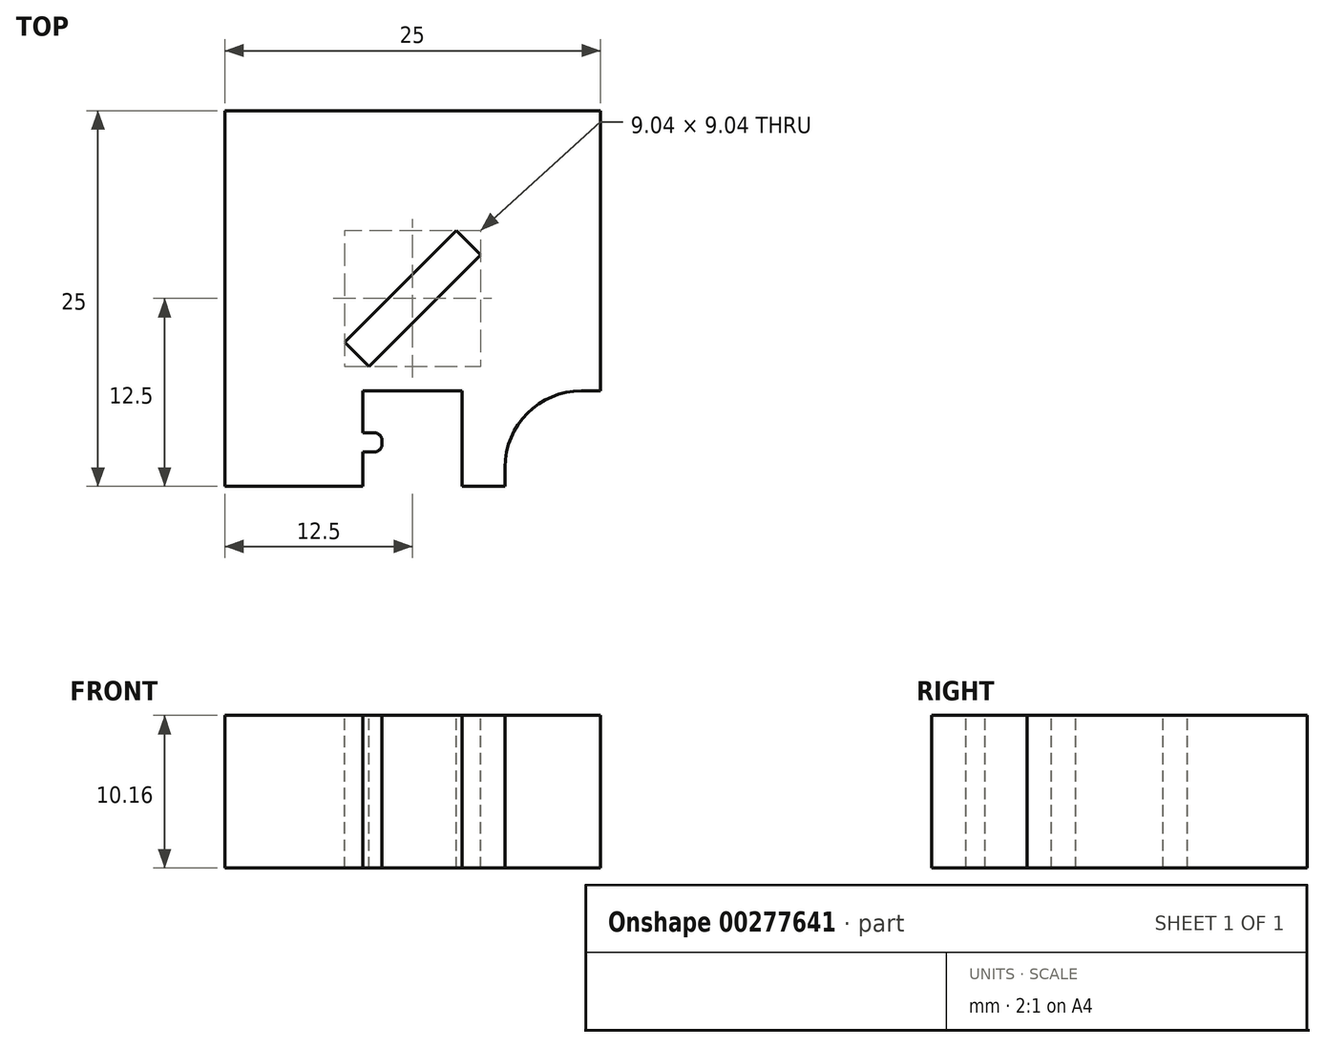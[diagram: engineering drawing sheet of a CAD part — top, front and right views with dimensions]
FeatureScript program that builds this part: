
annotation { "Feature Type Name" : "Feature", "Feature Type Description" : "" }
export const myFeature = defineFeature(function(context is Context, id is Id, definition is map)
    precondition{}
    {
        {
            var Q0;
            Q0=qCreatedBy(makeId("Top.planeOp"),FACE);
            var sketch = newSketch(context, id + "F0", { "sketchPlane" : qUnion([Q0])});
            skLineSegment(sketch, "E0.bottom", {"start": v(12.5, -12.5) * mm, "end": v(-12.5, -12.5) * mm});
            skLineSegment(sketch, "E0.top", {"start": v(12.5, 12.5) * mm, "end": v(-12.5, 12.5) * mm});
            skLineSegment(sketch, "E0.left", {"start": v(12.5, -12.5) * mm, "end": v(12.5, 12.5) * mm});
            skLineSegment(sketch, "E0.right", {"start": v(-12.5, -12.5) * mm, "end": v(-12.5, 12.5) * mm});
            skPoint(sketch, "E0.middle", {"position": v(0, 0) * mm});
            skSolve(sketch);
        }
        {
            var Q0;
            Q0=makeQuery(id+"F0.imprint","IMPRINT",FACE,{"disambiguationData":[TD([[makeQuery(id+"F0.imprint","IMPRINT",EDGE,{"derivedFrom":sQuery(id+"F0.wireOp",EDGE,"E0.bottom")}),-1.0]])]});
            extrude(context, id + "F1", {"entities" : qUnion([Q0]), "depth" : 10.16 * mm});
        }
        {
            var Q0;
            Q0=makeQuery(id+"F1.opExtrude","CAP_FACE",FACE,{"disambiguationData":[OSD([sQuery(id+"F0.wireOp",EDGE,"E0.bottom"),sQuery(id+"F0.wireOp",EDGE,"E0.top"),sQuery(id+"F0.wireOp",EDGE,"E0.left"),sQuery(id+"F0.wireOp",EDGE,"E0.right")])],"isStart":false});
            var sketch = newSketch(context, id + "F2", { "sketchPlane" : qUnion([Q0])});
            skLineSegment(sketch, "E1.bottom", {"start": v(-3.3, -12.5) * mm, "end": v(3.3, -12.5) * mm});
            skLineSegment(sketch, "E1.top", {"start": v(-3.3, -6.15) * mm, "end": v(3.3, -6.15) * mm});
            skLineSegment(sketch, "E1.left", {"start": v(-3.3, -12.5) * mm, "end": v(-3.3, -6.15) * mm});
            skLineSegment(sketch, "E1.right", {"start": v(3.3, -12.5) * mm, "end": v(3.3, -6.15) * mm});
            skSolve(sketch);
        }
        {
            var Q0;
            Q0=makeQuery(id+"F2.imprint","IMPRINT",FACE,{"disambiguationData":[TD([[makeQuery(id+"F2.imprint","IMPRINT",EDGE,{"derivedFrom":sQuery(id+"F2.wireOp",EDGE,"E1.bottom")}),-1.0]])]});
            extrude(context, id + "F3", {"entities" : qUnion([Q0]), "operationType" : NewBodyOperationType.REMOVE, "oppositeDirection" : true, "depth" : 25.4 * mm});
        }
        {
            var Q0;
            Q0=makeQuery(id+"F1.opExtrude","CAP_FACE",FACE,{"disambiguationData":[OSD([sQuery(id+"F0.wireOp",EDGE,"E0.bottom"),sQuery(id+"F0.wireOp",EDGE,"E0.top"),sQuery(id+"F0.wireOp",EDGE,"E0.left"),sQuery(id+"F0.wireOp",EDGE,"E0.right")])],"isStart":false});
            var sketch = newSketch(context, id + "F4", { "sketchPlane" : qUnion([Q0])});
            skLineSegment(sketch, "E2.bottom", {"start": v(-3.3, -8.94) * mm, "end": v(-2.03, -8.94) * mm});
            skLineSegment(sketch, "E2.top", {"start": v(-3.3, -10.21) * mm, "end": v(-2.03, -10.21) * mm});
            skLineSegment(sketch, "E2.left", {"start": v(-3.3, -8.94) * mm, "end": v(-3.3, -10.21) * mm});
            skLineSegment(sketch, "E2.right", {"start": v(-2.03, -8.94) * mm, "end": v(-2.03, -10.21) * mm});
            skSolve(sketch);
        }
        {
            var Q0;
            Q0=makeQuery(id+"F4.imprint","IMPRINT",FACE,{"disambiguationData":[TD([[makeQuery(id+"F4.imprint","IMPRINT",EDGE,{"derivedFrom":sQuery(id+"F4.wireOp",EDGE,"E2.bottom")}),-1.0]])]});
            var Q1;
            Q1=makeQuery(id+"F1.opExtrude","CAP_FACE",FACE,{"disambiguationData":[OSD([sQuery(id+"F0.wireOp",EDGE,"E0.bottom"),sQuery(id+"F0.wireOp",EDGE,"E0.top"),sQuery(id+"F0.wireOp",EDGE,"E0.left"),sQuery(id+"F0.wireOp",EDGE,"E0.right")])],"isStart":true});
            extrude(context, id + "F5", {"entities" : qUnion([Q0]), "operationType" : NewBodyOperationType.ADD, "endBound" : BoundingType.UP_TO_SURFACE, "oppositeDirection" : true, "endBoundEntityFace" : qUnion([Q1]), "depth" : 25.4 * mm});
        }
        {
            var Q0;
            Q0=qCreatedBy(makeId("Front.planeOp"),FACE);
            var sketch = newSketch(context, id + "F6", { "sketchPlane" : qUnion([Q0])});
            skLineSegment(sketch, "E3", {"start": v(0, 0) * mm, "end": v(0, 39.35) * mm});
            skSolve(sketch);
        }
        {
            var Q0;
            {var subQ0=sQuery(id+"F4.wireOp",EDGE,"E2.right");var subQ1=sQuery(id+"F4.wireOp",EDGE,"E2.left");var subQ2=sQuery(id+"F4.wireOp",EDGE,"E2.top");var subQ3=sQuery(id+"F4.wireOp",EDGE,"E2.bottom");Q0=makeQuery(id+"FZ99muYWaTXzHZh_1.3.F9qQpSXjTnUJ7Ic_1.1.F5.boolean.opBoolean","MERGE",FACE,{"derivedFrom":[makeQuery(id+"FZ99muYWaTXzHZh_1.3.F5.boolean.opBoolean","MERGE",FACE,{"derivedFrom":[makeQuery(id+"FZ99muYWaTXzHZh_1.2.F9qQpSXjTnUJ7Ic_1.1.F5.boolean.opBoolean","MERGE",FACE,{"derivedFrom":[makeQuery(id+"FZ99muYWaTXzHZh_1.2.F5.boolean.opBoolean","MERGE",FACE,{"derivedFrom":[makeQuery(id+"FZ99muYWaTXzHZh_1.1.F5.boolean.opBoolean","MERGE",FACE,{"derivedFrom":[makeQuery(id+"F9qQpSXjTnUJ7Ic_1.1.F5.boolean.opBoolean","MERGE",FACE,{"derivedFrom":[makeQuery(id+"F5.boolean.opBoolean","MERGE",FACE,{"derivedFrom":[makeQuery(id+"F1.opExtrude","CAP_FACE",FACE,{"disambiguationData":[OSD([sQuery(id+"F0.wireOp",EDGE,"E0.bottom"),sQuery(id+"F0.wireOp",EDGE,"E0.top"),sQuery(id+"F0.wireOp",EDGE,"E0.left"),sQuery(id+"F0.wireOp",EDGE,"E0.right")])],"isStart":false}),makeQuery(id+"F5.opExtrude","CAP_FACE",FACE,{"disambiguationData":[OSD([subQ3,subQ2,subQ1,subQ0])],"isStart":true})]}),makeQuery(id+"F9qQpSXjTnUJ7Ic_1.1.F5.opExtrude","CAP_FACE",FACE,{"disambiguationData":[OSD([subQ3,subQ2,subQ1,subQ0])],"isStart":true})]}),makeQuery(id+"FZ99muYWaTXzHZh_1.1.F5.opExtrude","CAP_FACE",FACE,{"disambiguationData":[OSD([subQ3,subQ2,subQ1,subQ0])],"isStart":true})]}),makeQuery(id+"FZ99muYWaTXzHZh_1.2.F5.opExtrude","CAP_FACE",FACE,{"disambiguationData":[OSD([subQ3,subQ2,subQ1,subQ0])],"isStart":true})]}),makeQuery(id+"FZ99muYWaTXzHZh_1.2.F9qQpSXjTnUJ7Ic_1.1.F5.opExtrude","CAP_FACE",FACE,{"disambiguationData":[OSD([subQ3,subQ2,subQ1,subQ0])],"isStart":true})]}),makeQuery(id+"FZ99muYWaTXzHZh_1.3.F5.opExtrude","CAP_FACE",FACE,{"disambiguationData":[OSD([subQ3,subQ2,subQ1,subQ0])],"isStart":true})]}),makeQuery(id+"FZ99muYWaTXzHZh_1.3.F9qQpSXjTnUJ7Ic_1.1.F5.opExtrude","CAP_FACE",FACE,{"disambiguationData":[OSD([subQ3,subQ2,subQ1,subQ0])],"isStart":true})]});}
            var sketch = newSketch(context, id + "F7", { "sketchPlane" : qUnion([Q0])});
            skLineSegment(sketch, "E4.bottom", {"start": v(-9.96, -3.3) * mm, "end": v(-8.7, -3.3) * mm});
            skLineSegment(sketch, "E4.top", {"start": v(-9.96, -2.03) * mm, "end": v(-8.7, -2.03) * mm});
            skLineSegment(sketch, "E4.left", {"start": v(-9.96, -3.3) * mm, "end": v(-9.96, -2.03) * mm});
            skLineSegment(sketch, "E4.right", {"start": v(-8.7, -3.3) * mm, "end": v(-8.7, -2.03) * mm});
            skSolve(sketch);
        }
        {
            var Q0;
            Q0=makeQuery(id+"F7.imprint","IMPRINT",FACE,{"disambiguationData":[TD([[makeQuery(id+"F7.imprint","IMPRINT",EDGE,{"derivedFrom":sQuery(id+"F7.wireOp",EDGE,"E4.bottom")}),1.0]])]});
            var Q1;
            {var subQ0=sQuery(id+"F0.wireOp",EDGE,"E0.right");var subQ1=sQuery(id+"F0.wireOp",EDGE,"E0.left");var subQ2=sQuery(id+"F0.wireOp",EDGE,"E0.top");var subQ3=sQuery(id+"F0.wireOp",EDGE,"E0.bottom");Q1=makeQuery(id+"FZ99muYWaTXzHZh_1.3.F9qQpSXjTnUJ7Ic_1.1.F5.boolean.opBoolean","MERGE",FACE,{"derivedFrom":[makeQuery(id+"FZ99muYWaTXzHZh_1.3.F5.boolean.opBoolean","MERGE",FACE,{"derivedFrom":[makeQuery(id+"FZ99muYWaTXzHZh_1.2.F9qQpSXjTnUJ7Ic_1.1.F5.boolean.opBoolean","MERGE",FACE,{"derivedFrom":[makeQuery(id+"FZ99muYWaTXzHZh_1.2.F5.boolean.opBoolean","MERGE",FACE,{"derivedFrom":[makeQuery(id+"FZ99muYWaTXzHZh_1.1.F5.boolean.opBoolean","MERGE",FACE,{"derivedFrom":[makeQuery(id+"F9qQpSXjTnUJ7Ic_1.1.F5.boolean.opBoolean","MERGE",FACE,{"derivedFrom":[makeQuery(id+"F5.boolean.opBoolean","MERGE",FACE,{"derivedFrom":[makeQuery(id+"F1.opExtrude","CAP_FACE",FACE,{"disambiguationData":[OSD([subQ3,subQ2,subQ1,subQ0])],"isStart":true}),makeQuery(id+"F5.opExtrude","CAP_FACE",FACE,{"disambiguationData":[OSD([subQ3,subQ2,subQ1,subQ0])],"isStart":false})]}),makeQuery(id+"F9qQpSXjTnUJ7Ic_1.1.F5.opExtrude","CAP_FACE",FACE,{"disambiguationData":[OSD([subQ3,subQ2,subQ1,subQ0])],"isStart":false})]}),makeQuery(id+"FZ99muYWaTXzHZh_1.1.F5.opExtrude","CAP_FACE",FACE,{"disambiguationData":[OSD([subQ3,subQ2,subQ1,subQ0])],"isStart":false})]}),makeQuery(id+"FZ99muYWaTXzHZh_1.2.F5.opExtrude","CAP_FACE",FACE,{"disambiguationData":[OSD([subQ3,subQ2,subQ1,subQ0])],"isStart":false})]}),makeQuery(id+"FZ99muYWaTXzHZh_1.2.F9qQpSXjTnUJ7Ic_1.1.F5.opExtrude","CAP_FACE",FACE,{"disambiguationData":[OSD([subQ3,subQ2,subQ1,subQ0])],"isStart":false})]}),makeQuery(id+"FZ99muYWaTXzHZh_1.3.F5.opExtrude","CAP_FACE",FACE,{"disambiguationData":[OSD([subQ3,subQ2,subQ1,subQ0])],"isStart":false})]}),makeQuery(id+"FZ99muYWaTXzHZh_1.3.F9qQpSXjTnUJ7Ic_1.1.F5.opExtrude","CAP_FACE",FACE,{"disambiguationData":[OSD([subQ3,subQ2,subQ1,subQ0])],"isStart":false})]});}
            extrude(context, id + "F8", {"entities" : qUnion([Q0]), "operationType" : NewBodyOperationType.ADD, "endBound" : BoundingType.UP_TO_SURFACE, "oppositeDirection" : true, "endBoundEntityFace" : qUnion([Q1]), "depth" : 25.4 * mm});
        }
        {
            var Q0;
            {var subQ0=sQuery(id+"F4.wireOp",EDGE,"E2.right");var subQ1=sQuery(id+"F4.wireOp",EDGE,"E2.left");var subQ2=sQuery(id+"F4.wireOp",EDGE,"E2.top");var subQ3=sQuery(id+"F4.wireOp",EDGE,"E2.bottom");Q0=makeQuery(id+"F8.boolean.opBoolean","MERGE",FACE,{"derivedFrom":[makeQuery(id+"FZ99muYWaTXzHZh_1.3.F9qQpSXjTnUJ7Ic_1.1.F5.boolean.opBoolean","MERGE",FACE,{"derivedFrom":[makeQuery(id+"FZ99muYWaTXzHZh_1.3.F5.boolean.opBoolean","MERGE",FACE,{"derivedFrom":[makeQuery(id+"FZ99muYWaTXzHZh_1.2.F9qQpSXjTnUJ7Ic_1.1.F5.boolean.opBoolean","MERGE",FACE,{"derivedFrom":[makeQuery(id+"FZ99muYWaTXzHZh_1.2.F5.boolean.opBoolean","MERGE",FACE,{"derivedFrom":[makeQuery(id+"FZ99muYWaTXzHZh_1.1.F5.boolean.opBoolean","MERGE",FACE,{"derivedFrom":[makeQuery(id+"F9qQpSXjTnUJ7Ic_1.1.F5.boolean.opBoolean","MERGE",FACE,{"derivedFrom":[makeQuery(id+"F5.boolean.opBoolean","MERGE",FACE,{"derivedFrom":[makeQuery(id+"F1.opExtrude","CAP_FACE",FACE,{"disambiguationData":[OSD([sQuery(id+"F0.wireOp",EDGE,"E0.bottom"),sQuery(id+"F0.wireOp",EDGE,"E0.top"),sQuery(id+"F0.wireOp",EDGE,"E0.left"),sQuery(id+"F0.wireOp",EDGE,"E0.right")])],"isStart":false}),makeQuery(id+"F5.opExtrude","CAP_FACE",FACE,{"disambiguationData":[OSD([subQ3,subQ2,subQ1,subQ0])],"isStart":true})]}),makeQuery(id+"F9qQpSXjTnUJ7Ic_1.1.F5.opExtrude","CAP_FACE",FACE,{"disambiguationData":[OSD([subQ3,subQ2,subQ1,subQ0])],"isStart":true})]}),makeQuery(id+"FZ99muYWaTXzHZh_1.1.F5.opExtrude","CAP_FACE",FACE,{"disambiguationData":[OSD([subQ3,subQ2,subQ1,subQ0])],"isStart":true})]}),makeQuery(id+"FZ99muYWaTXzHZh_1.2.F5.opExtrude","CAP_FACE",FACE,{"disambiguationData":[OSD([subQ3,subQ2,subQ1,subQ0])],"isStart":true})]}),makeQuery(id+"FZ99muYWaTXzHZh_1.2.F9qQpSXjTnUJ7Ic_1.1.F5.opExtrude","CAP_FACE",FACE,{"disambiguationData":[OSD([subQ3,subQ2,subQ1,subQ0])],"isStart":true})]}),makeQuery(id+"FZ99muYWaTXzHZh_1.3.F5.opExtrude","CAP_FACE",FACE,{"disambiguationData":[OSD([subQ3,subQ2,subQ1,subQ0])],"isStart":true})]}),makeQuery(id+"FZ99muYWaTXzHZh_1.3.F9qQpSXjTnUJ7Ic_1.1.F5.opExtrude","CAP_FACE",FACE,{"disambiguationData":[OSD([subQ3,subQ2,subQ1,subQ0])],"isStart":true})]}),makeQuery(id+"F8.opExtrude","CAP_FACE",FACE,{"disambiguationData":[OSD([sQuery(id+"F7.wireOp",EDGE,"E4.bottom"),sQuery(id+"F7.wireOp",EDGE,"E4.top"),sQuery(id+"F7.wireOp",EDGE,"E4.left"),sQuery(id+"F7.wireOp",EDGE,"E4.right")])],"isStart":true})]});}
            var sketch = newSketch(context, id + "F9", { "sketchPlane" : qUnion([Q0])});
            skLineSegment(sketch, "E5.bottom", {"start": v(12.5, -12.5) * mm, "end": v(6.15, -12.5) * mm});
            skLineSegment(sketch, "E5.top", {"start": v(12.5, -6.15) * mm, "end": v(6.15, -6.15) * mm});
            skLineSegment(sketch, "E5.left", {"start": v(12.5, -12.5) * mm, "end": v(12.5, -6.15) * mm});
            skLineSegment(sketch, "E5.right", {"start": v(6.15, -12.5) * mm, "end": v(6.15, -6.15) * mm});
            skSolve(sketch);
        }
        {
            var Q0;
            Q0=makeQuery(id+"F9.imprint","IMPRINT",FACE,{"disambiguationData":[TD([[makeQuery(id+"F9.imprint","IMPRINT",EDGE,{"derivedFrom":sQuery(id+"F9.wireOp",EDGE,"E5.bottom")}),-1.0]])]});
            extrude(context, id + "F10", {"entities" : qUnion([Q0]), "operationType" : NewBodyOperationType.REMOVE, "oppositeDirection" : true, "depth" : 25.4 * mm});
        }
        {
            var Q0;
            Q0=makeQuery(id+"F10.boolean.opBoolean","COPY",EDGE,{"derivedFrom":makeQuery(id+"F10.opExtrude","SWEPT_EDGE",EDGE,{"disambiguationData":[OSD([sQuery(id+"F9.wireOp",EDGE,"E5.top"),sQuery(id+"F9.wireOp",EDGE,"E5.right")])]})});
            fillet(context, id + "F11", {"entities" : qUnion([Q0]), "radius" : 5.08 * mm, "tangentPropagation" : true, "allowEdgeOverflow" : false});
        }
        {
            var Q0;
            {var subQ44=sQuery(id+"F7.wireOp",EDGE,"E4.bottom");Q0=makeQuery(id+"F7.imprint","IMPRINT",FACE,{"disambiguationData":[TD([[makeQuery(id+"F7.imprint","IMPRINT",EDGE,{"derivedFrom":subQ44}),-1.0]])]});}
            var sketch = newSketch(context, id + "F12", { "sketchPlane" : qUnion([Q0])});
            skLineSegment(sketch, "E6", {"start": v(-4.52, -2.9) * mm, "end": v(2.9, 4.52) * mm});
            skLineSegment(sketch, "E7", {"start": v(2.9, 4.52) * mm, "end": v(4.52, 2.9) * mm});
            skLineSegment(sketch, "E8", {"start": v(4.52, 2.9) * mm, "end": v(-2.9, -4.52) * mm});
            skLineSegment(sketch, "E9", {"start": v(-2.9, -4.52) * mm, "end": v(-4.52, -2.9) * mm});
            skLineSegment(sketch, "E10", {"start": v(-3.71, -3.71) * mm, "end": v(0, 0) * mm});
            skLineSegment(sketch, "E11", {"start": v(-0.8, 0.8) * mm, "end": v(0, 0) * mm});
            skSolve(sketch);
        }
        {
            var Q0;
            Q0 = qSketchRegion(id + "F12", true);
            extrude(context, id + "F13", {"entities" : qUnion([Q0]), "operationType" : NewBodyOperationType.REMOVE, "oppositeDirection" : true, "depth" : 25.4 * mm});
        }
        {
            var Q0;
            Q0=makeQuery(id+"FZ99muYWaTXzHZh_1.3.F9qQpSXjTnUJ7Ic_1.1.F5.opExtrude","SWEPT_EDGE",EDGE,{"disambiguationData":[OSD([sQuery(id+"F4.wireOp",EDGE,"E2.top"),sQuery(id+"F4.wireOp",EDGE,"E2.right")])]});
            var Q1;
            Q1=makeQuery(id+"FZ99muYWaTXzHZh_1.3.F9qQpSXjTnUJ7Ic_1.1.F5.opExtrude","SWEPT_EDGE",EDGE,{"disambiguationData":[OSD([sQuery(id+"F4.wireOp",EDGE,"E2.bottom"),sQuery(id+"F4.wireOp",EDGE,"E2.right")])]});
            var Q2;
            Q2=makeQuery(id+"FZ99muYWaTXzHZh_1.1.F5.opExtrude","SWEPT_EDGE",EDGE,{"disambiguationData":[OSD([sQuery(id+"F4.wireOp",EDGE,"E2.bottom"),sQuery(id+"F4.wireOp",EDGE,"E2.right")])]});
            var Q3;
            Q3=makeQuery(id+"FZ99muYWaTXzHZh_1.1.F5.opExtrude","SWEPT_EDGE",EDGE,{"disambiguationData":[OSD([sQuery(id+"F4.wireOp",EDGE,"E2.top"),sQuery(id+"F4.wireOp",EDGE,"E2.right")])]});
            var Q4;
            Q4=makeQuery(id+"F9qQpSXjTnUJ7Ic_1.1.F5.opExtrude","SWEPT_EDGE",EDGE,{"disambiguationData":[OSD([sQuery(id+"F4.wireOp",EDGE,"E2.bottom"),sQuery(id+"F4.wireOp",EDGE,"E2.right")])]});
            var Q5;
            Q5=makeQuery(id+"F9qQpSXjTnUJ7Ic_1.1.F5.opExtrude","SWEPT_EDGE",EDGE,{"disambiguationData":[OSD([sQuery(id+"F4.wireOp",EDGE,"E2.top"),sQuery(id+"F4.wireOp",EDGE,"E2.right")])]});
            var Q6;
            Q6=makeQuery(id+"F5.opExtrude","SWEPT_EDGE",EDGE,{"disambiguationData":[OSD([sQuery(id+"F4.wireOp",EDGE,"E2.top"),sQuery(id+"F4.wireOp",EDGE,"E2.right")])]});
            var Q7;
            Q7=makeQuery(id+"F5.opExtrude","SWEPT_EDGE",EDGE,{"disambiguationData":[OSD([sQuery(id+"F4.wireOp",EDGE,"E2.bottom"),sQuery(id+"F4.wireOp",EDGE,"E2.right")])]});
            var Q8;
            Q8=makeQuery(id+"FZ99muYWaTXzHZh_1.2.F9qQpSXjTnUJ7Ic_1.1.F5.opExtrude","SWEPT_EDGE",EDGE,{"disambiguationData":[OSD([sQuery(id+"F4.wireOp",EDGE,"E2.top"),sQuery(id+"F4.wireOp",EDGE,"E2.right")])]});
            var Q9;
            Q9=makeQuery(id+"FZ99muYWaTXzHZh_1.2.F9qQpSXjTnUJ7Ic_1.1.F5.opExtrude","SWEPT_EDGE",EDGE,{"disambiguationData":[OSD([sQuery(id+"F4.wireOp",EDGE,"E2.bottom"),sQuery(id+"F4.wireOp",EDGE,"E2.right")])]});
            var Q10;
            Q10=makeQuery(id+"FZ99muYWaTXzHZh_1.2.F5.opExtrude","SWEPT_EDGE",EDGE,{"disambiguationData":[OSD([sQuery(id+"F4.wireOp",EDGE,"E2.top"),sQuery(id+"F4.wireOp",EDGE,"E2.right")])]});
            var Q11;
            Q11=makeQuery(id+"FZ99muYWaTXzHZh_1.2.F5.opExtrude","SWEPT_EDGE",EDGE,{"disambiguationData":[OSD([sQuery(id+"F4.wireOp",EDGE,"E2.bottom"),sQuery(id+"F4.wireOp",EDGE,"E2.right")])]});
            var Q12;
            Q12=makeQuery(id+"FZ99muYWaTXzHZh_1.3.F5.opExtrude","SWEPT_EDGE",EDGE,{"disambiguationData":[OSD([sQuery(id+"F4.wireOp",EDGE,"E2.top"),sQuery(id+"F4.wireOp",EDGE,"E2.right")])]});
            var Q13;
            Q13=makeQuery(id+"FZ99muYWaTXzHZh_1.3.F5.opExtrude","SWEPT_EDGE",EDGE,{"disambiguationData":[OSD([sQuery(id+"F4.wireOp",EDGE,"E2.bottom"),sQuery(id+"F4.wireOp",EDGE,"E2.right")])]});
            var Q14;
            Q14=makeQuery(id+"F8.opExtrude","SWEPT_EDGE",EDGE,{"disambiguationData":[OSD([sQuery(id+"F7.wireOp",EDGE,"E4.top"),sQuery(id+"F7.wireOp",EDGE,"E4.left")])]});
            var Q15;
            Q15=makeQuery(id+"F8.opExtrude","SWEPT_EDGE",EDGE,{"disambiguationData":[OSD([sQuery(id+"F7.wireOp",EDGE,"E4.top"),sQuery(id+"F7.wireOp",EDGE,"E4.right")])]});
            fillet(context, id + "F14", {"entities" : qUnion([Q0, Q1, Q2, Q3, Q4, Q5, Q6, Q7, Q8, Q9, Q10, Q11, Q12, Q13, Q14, Q15]), "radius" : 0.5 * mm, "tangentPropagation" : true, "allowEdgeOverflow" : false});
        }
    });
